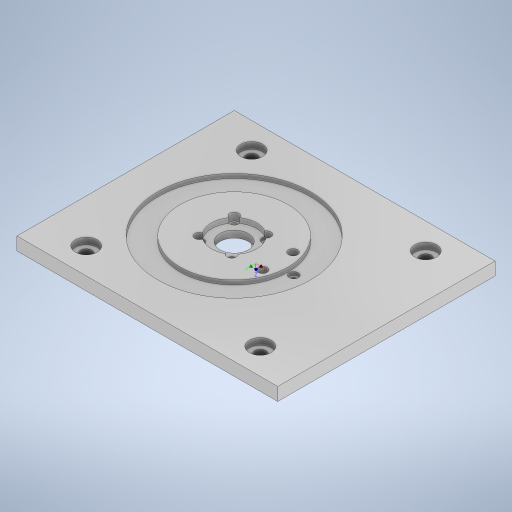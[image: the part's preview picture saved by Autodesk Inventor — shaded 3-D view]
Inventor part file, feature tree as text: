
AUTODESK INVENTOR PART (.ipt)
format: ipt  version: 2024.2 (Build 282272000, 272)  size: 535,040 bytes
history: native  units: in
note: dims shown in document units (in); Inventor stores cm internally (conversion verified against a paired STEP export)
features: reference x14, sketch x8, extrude x6, other x5, hole x2
ambient origin geometry x8: Origin, YZ Plane, XZ Plane, XY Plane, X Axis, Y Axis, Z Axis, Center Point
bodies: Solid1 (feature_tree)
feature tree (35):
  extrude  "Extrusion1"  Depth=3.937in
  extrude  "Extrusion3"  Depth=0.2362in
  hole  "Hole1"  [1 undecoded]
  extrude  "Extrusion6"  Depth=0.1378in
  extrude  "Extrusion9"  Depth=0.0787in TaperAngle=0.0deg
  hole  "Hole2"  [1 undecoded]
  extrude  "Extrusion10"  Depth=0.7929in
  extrude  "Extrusion11"  Depth=0.3937in
  sketch  "Sketch1"  dims[d0=4.7244in d1=3.937in]
  sketch  "Sketch5"  dims[d2=0.2362in d3=0.0in d16=0.8189in]
  reference  "Reference22"
  sketch  "Sketch6"  dims[d17=0.0906in d18=0.0in]
  reference  "Reference23"
  reference  "Reference24"
  reference  "Reference25"
  reference  "Reference26"
  reference  "Reference27"
  reference  "Reference28"
  reference  "Reference29"
  sketch  "Sketch8"  dims[d21=0.0827in d22=0.1575in d23=0.1732in d24=0.0787in d25=90.0deg d26=0.315in d27=0.0in d31=0.1614in]
  sketch  "Sketch11"  dims[d32=0.1378in d33=0.0in d38=0.0059in]
  reference  "Reference30"
  reference  "Reference31"
  sketch  "Sketch12"  dims[d39=0.0059in d40=0.0787in d41=0.0in]
  reference  "Reference32"
  reference  "Reference33"
  reference  "Reference34"
  reference  "Reference35"
  sketch  "Sketch13"  dims[d42=0.4724in]
  sketch  "Sketch14"  dims[d43=0.2047in d44=0.2362in d45=0.3937in d46=0.1181in d47=0.5635in d48=0.315in d49=0.8108in d50=1.5787in d51=0.7929in d52=0.3937in d53=0.0394in d54=0.0197in d55=0.0in d56=0.5118in d57=0.0in d58=0.0in d19=0.0344in d20=0.0344in]
  other  "2_Arm.iam"
  other  "HTD-45H:1"
  other  "AXK5070+AS Bearing:1"
  other  "Aluminum_Profile_4040_100.14mm_top:1"
  other  "Aluminum_Profile_4040_100.14mm_bottom:1"
note: 2 required parameter values undecoded (feature->parameter linkage not recoverable at this tier; creation-order binding heuristic only, values carry confidence <= 0.55)
